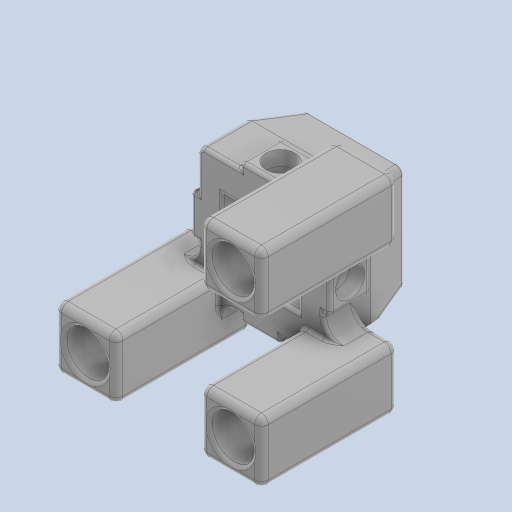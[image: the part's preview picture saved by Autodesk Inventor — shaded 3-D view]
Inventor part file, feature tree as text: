
AUTODESK INVENTOR PART (.ipt)
format: ipt  version: 2023 (Build 270158000, 158)  size: 1,595,392 bytes
history: native  units: mm
features: other x20, extrude x7, fillet x4, projected_geometry x2, chamfer x1, pattern_circular x1
ambient origin geometry x8: Origin, YZ Plane, XZ Plane, XY Plane, X Axis, Y Axis, Z Axis, Center Point
bodies: Solid1 (feature_tree)
feature tree (35):
  other  "Universal_ConstructorHead.ipt"
  other  "NP2-Alpha_Docking.ipt"
  extrude  "Ex:Side1"  Depth=10.0mm TaperAngle=0.0deg
  other  "Sk:Side2"
  extrude  "Ex:RemoveExcess"  Depth=15.0mm TaperAngle=0.0deg
  extrude  "Ex:Side2"  Depth=15.0mm TaperAngle=0.0deg
  other  "Sk:PostHolder"
  extrude  "Ex:PostHolder"  Depth=15.0mm TaperAngle=0.0deg
  other  "TopCuffPlane"
  fillet  "Fillet:PostHolder1"  Radius=5.0mm
  fillet  "Fillet:PostHolder2"  Radius=10.0mm
  extrude  "Ex:PostHolderHole"  Depth=10.0mm
  other  "SideSketchPlane"
  other  "Sk:ThreadInsert"
  extrude  "Ex:ThreadHole"  Depth=4.0mm
  extrude  "Ex:ThreadInsert"  TaperAngle=0.0deg  [1 undecoded]
  fillet  "Fillet:ThreadInsert"  [1 undecoded]
  chamfer  "Chamfer:ThreadInsert"  Distance=0.8mm
  pattern_circular  "Pat:ThreadInsert"  [2 undecoded]
  fillet  "Filltet:Final"  Radius=1.15mm
  other  "Sk:Side1"
  other  "TaggingFeature2"
  other  "TaggingFeature4"
  other  "EndPlane_1"
  other  "AnglePlane2"
  other  "AnglePlane1_1"
  other  "FrontPlane"
  other  "SidePlane1"
  other  "SidePlane2"
  projected_geometry  "Projected Loop2"
  projected_geometry  "Projected Loop3"
  other  "Solid1::Universal_ConstructorHead.ipt"
  other  "Srf2"
  other  "Solid1::NP2-Alpha_Docking.ipt"
  other  "Srf3"
note: 4 required parameter values undecoded (feature->parameter linkage not recoverable at this tier; creation-order binding heuristic only, values carry confidence <= 0.55)
